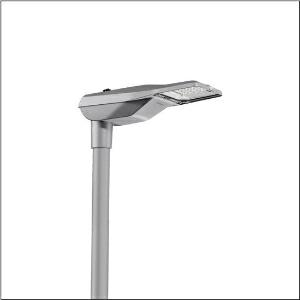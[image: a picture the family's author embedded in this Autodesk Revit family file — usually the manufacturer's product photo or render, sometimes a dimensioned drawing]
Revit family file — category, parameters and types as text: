
# Revit family: streetlight_sl_21_iq_micro___st1_0a_5xe1d31v08cb_77a3
name_source: partatom
category: Lighting Fixtures
units: mm (PartAtom-declared; Revit-internal decimal feet)

## family parameters
Cut with Voids When Loaded = No
Host = Face
Light Source = No
Part Type = Normal
Room Calculation Point = No
Round Connector Dimension = Use Diameter
Shared = No

## types (1)
- --- (1 x LED, 2880 lm, 19.1 W, 3000K)
    Apparent Load = 19 VA
    CIE Flux Codes = 37 72 97 100 100
    Color Rendering = 70
    Color Temperature = 3000K
    Default Elevation = 1800 mm
    Description = Streetlight SL 21 iQ micro, mast luminaire, primary light control with lens, of PMMA, primary optical cover: cover, of toughened safety glass, transparent, light distribution: ST1.0a, light emission: direct distribution, primary light characteristic: asymmetric, installation type: post-top, side-entry, LED, High Power LED, rated luminous flux: 2.880lm, luminous efficacy: 151lm/W, light colour: 730, colour temperature: 3000K, control: presetting dimming logarithmic, Street-Remote, Auto-Match, Temp-Guard, Lumen-Switch, Night-Set, Smart-Wire, Light-Fading, Desk-Remote (wireless, voltage-free reading and setting of iQ features in the workshop via application-optimized NFC function/RFID function), optimised constant luminous flux control (CLO 2.0), mains connection: 220..240V, AC, 50/60Hz, start of lifetime: 19W, end of service life: 20W, reduction: 9W, luminaire housing, of diecast aluminium, powder-coated, Siteco® metallic grey (DB 702S), corrosivity category C5 mid according to DIN EN ISO 12944, please order mast flange separately, inclination adjustable: 0°, 5°, 10°, 15°, sealing non-destructively replaceable, multi-level sealing system, length: 528mm, width: 235mm, height: 110mm, mast flange for spigot size: 42mm (side-entry): 5XC10008XM4, 60/48mm (side-entry/post-top): 5XC10108XM2, 76/60mm (side-entry/post-top): 5XC10108XM1, Smart Interface above, protection rating (complete): IP66, insulation class (complete): insulation class II (safety insulation), certification: CE, ENEC, ENEC+, VDE, impact resistance: IK09, permissible operating ambient temperature for outdoor applications: -40..+50°C, standard-compliant lighting for roads and squares, packaging unit: 1 piece

Light Distribution: ST1.0a
    Height = 110 mm
    Lamp = 1 x LED
    Lamp Light Flux = 2880 lm
    Lamp Power = 19.1 W
    Lamp count = 1
    Length = 528 mm
    Luminous efficacy = 151 lm/W
    Manufacturer = Siteco
    ModVariant = No
    Model = 5XE1D31V08CB
    Number of Poles = 1
    OnlyDefault = Yes
    Power Factor = 1
    Product Name = Streetlight SL 21 iQ micro | ST1.0a
    Product group = mast luminaire | pylon top
    ProductGroupID = 6100
    Protection Class = Protection class II
    Protection Degree = IP 66
    RLX_Detail_Level = 1
    RLX_Emergency_Light_Flux = 0 lm
    RLX_Emergency_Type = 0
    RLX_Emergency_Type_DB = No
    RlxData = <blob elided: 98773 chars, md5=26ff1428>
    Socket = socket
    Standby Power = 0 W
    System Light Flux = 2880 lm
    System Power = 19 W
    Type Comments = factory setting: luminous flux: 100 % | dim-lin: 254 | 387 mA
    Type Image = l_1277292.jpg
    URL = http://relux.com
    VarID = @adj_045723
    Voltage = 0 V
    Weight = 0.00 kg
    Width = 235 mm

## geometry (parser evidence)
native form markers: Blend x4, Sweep x9
no freeform markers — native parametric forms only
